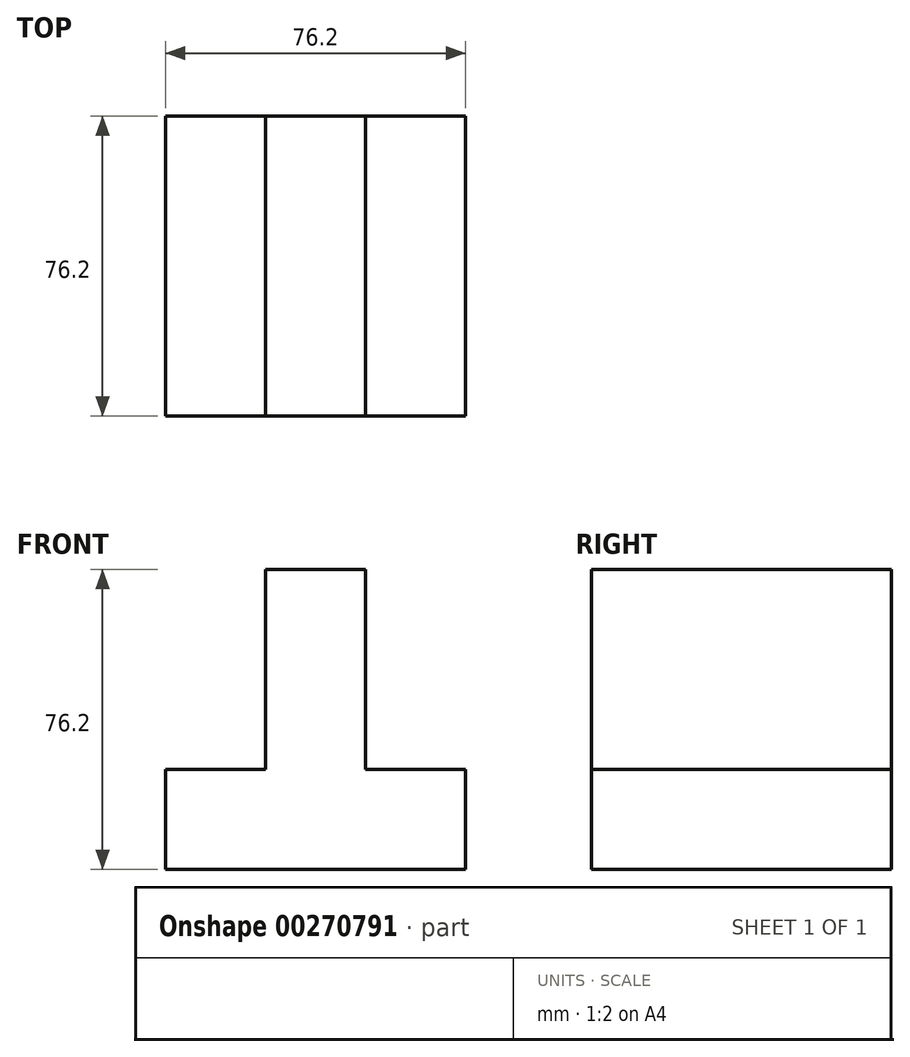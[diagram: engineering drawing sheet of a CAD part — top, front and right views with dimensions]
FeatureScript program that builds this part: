
annotation { "Feature Type Name" : "Feature", "Feature Type Description" : "" }
export const myFeature = defineFeature(function(context is Context, id is Id, definition is map)
    precondition{}
    {
        {
            var Q0;
            Q0=qCreatedBy(makeId("Front.planeOp"),FACE);
            var sketch = newSketch(context, id + "F0", { "sketchPlane" : qUnion([Q0])});
            skLineSegment(sketch, "E0", {"start": v(-42.25, -18.43) * mm, "end": v(33.95, -18.43) * mm});
            skLineSegment(sketch, "E1", {"start": v(33.95, -18.43) * mm, "end": v(33.95, 6.97) * mm});
            skLineSegment(sketch, "E2", {"start": v(33.95, 6.97) * mm, "end": v(8.55, 6.97) * mm});
            skLineSegment(sketch, "E3", {"start": v(8.55, 6.97) * mm, "end": v(8.55, 57.77) * mm});
            skLineSegment(sketch, "E4", {"start": v(8.55, 57.77) * mm, "end": v(-16.85, 57.77) * mm});
            skLineSegment(sketch, "E5", {"start": v(-16.85, 57.77) * mm, "end": v(-16.85, 6.97) * mm});
            skLineSegment(sketch, "E6", {"start": v(-16.85, 6.97) * mm, "end": v(-42.25, 6.97) * mm});
            skLineSegment(sketch, "E7", {"start": v(-42.25, 6.97) * mm, "end": v(-42.25, -18.43) * mm});
            skSolve(sketch);
        }
        {
            var Q0;
            Q0 = qSketchRegion(id + "F0", true);
            extrude(context, id + "F1", {"entities" : qUnion([Q0]), "depth" : 76.2 * mm});
        }
    });
